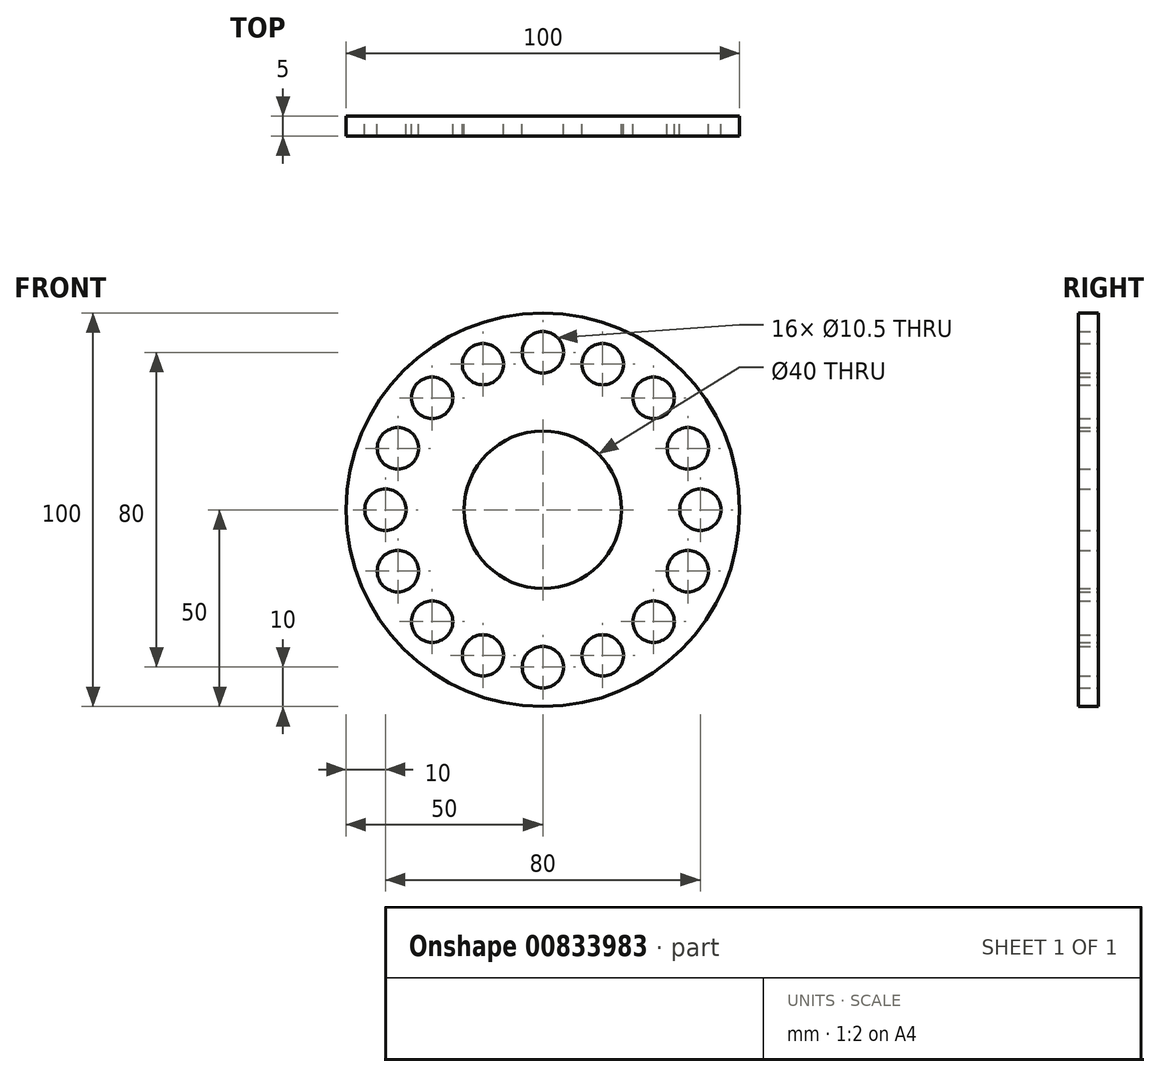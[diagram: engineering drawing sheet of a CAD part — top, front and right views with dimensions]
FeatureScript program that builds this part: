
annotation { "Feature Type Name" : "Feature", "Feature Type Description" : "" }
export const myFeature = defineFeature(function(context is Context, id is Id, definition is map)
    precondition{}
    {
        {
            var Q0;
            Q0=qCreatedBy(makeId("Front.planeOp"),FACE);
            var sketch = newSketch(context, id + "F0", { "sketchPlane" : qUnion([Q0])});
            skCircle(sketch, "E0", {"center": v(0, 0) * mm, "radius": 50 * mm});
            skCircle(sketch, "E1", {"center": v(0, 0) * mm, "radius": 20 * mm});
            skPoint(sketch, "E2", {"position": v(0, 40) * mm});
            skPoint(sketch, "E3", {"position": v(-40, 0) * mm});
            skPoint(sketch, "E4", {"position": v(0, -40) * mm});
            skPoint(sketch, "E5", {"position": v(40, 0) * mm});
            skPoint(sketch, "E6", {"position": v(15.2, 37) * mm});
            skPoint(sketch, "E7", {"position": v(28.13, 28.44) * mm});
            skPoint(sketch, "E8", {"position": v(36.83, 15.6) * mm});
            skPoint(sketch, "E9.MirrorP", {"position": v(-36.83, 15.6) * mm});
            skPoint(sketch, "E10.MirrorP", {"position": v(-15.2, 37) * mm});
            skPoint(sketch, "E11.MirrorP", {"position": v(-28.13, 28.44) * mm});
            skPoint(sketch, "E12.MirrorP", {"position": v(-28.13, -28.44) * mm});
            skPoint(sketch, "E13.MirrorP", {"position": v(-36.83, -15.6) * mm});
            skPoint(sketch, "E14.MirrorP", {"position": v(15.2, -37) * mm});
            skPoint(sketch, "E15.MirrorP", {"position": v(-15.2, -37) * mm});
            skPoint(sketch, "E16.MirrorP", {"position": v(28.13, -28.44) * mm});
            skPoint(sketch, "E17.MirrorP", {"position": v(36.83, -15.6) * mm});
            skCircle(sketch, "E18", {"center": v(-15.2, 37) * mm, "radius": 5.25 * mm});
            skCircle(sketch, "E19", {"center": v(-28.13, 28.44) * mm, "radius": 5.25 * mm});
            skCircle(sketch, "E20", {"center": v(-36.83, 15.6) * mm, "radius": 5.25 * mm});
            skCircle(sketch, "E21", {"center": v(-40, 0) * mm, "radius": 5.25 * mm});
            skCircle(sketch, "E22", {"center": v(0, 40) * mm, "radius": 5.25 * mm});
            skCircle(sketch, "E23", {"center": v(15.2, 37) * mm, "radius": 5.25 * mm});
            skCircle(sketch, "E24", {"center": v(28.13, 28.44) * mm, "radius": 5.25 * mm});
            skCircle(sketch, "E25", {"center": v(36.83, 15.6) * mm, "radius": 5.25 * mm});
            skCircle(sketch, "E26", {"center": v(40, 0) * mm, "radius": 5.25 * mm});
            skCircle(sketch, "E27.MirrorC", {"center": v(36.83, -15.6) * mm, "radius": 5.25 * mm});
            skCircle(sketch, "E28.MirrorC", {"center": v(15.2, -37) * mm, "radius": 5.25 * mm});
            skCircle(sketch, "E29.MirrorC", {"center": v(-15.2, -37) * mm, "radius": 5.25 * mm});
            skCircle(sketch, "E30.MirrorC", {"center": v(28.13, -28.44) * mm, "radius": 5.25 * mm});
            skCircle(sketch, "E31.MirrorC", {"center": v(-36.83, -15.6) * mm, "radius": 5.25 * mm});
            skCircle(sketch, "E32.MirrorC", {"center": v(0, -40) * mm, "radius": 5.25 * mm});
            skCircle(sketch, "E33.MirrorC", {"center": v(-28.13, -28.44) * mm, "radius": 5.25 * mm});
            skSolve(sketch);
        }
        {
            var Q0;
            Q0=makeQuery(id+"F0.imprint","IMPRINT",FACE,{"disambiguationData":[TD([[makeQuery(id+"F0.imprint","IMPRINT",EDGE,{"derivedFrom":sQuery(id+"F0.wireOp",EDGE,"E0")}),1.0]])]});
            var Q1;
            Q1=makeQuery(id+"F0.imprint","IMPRINT",FACE,{"disambiguationData":[TD([[makeQuery(id+"F0.imprint","IMPRINT",EDGE,{"derivedFrom":sQuery(id+"F0.wireOp",EDGE,"E1")}),-1.0]])]});
            extrude(context, id + "F1", {"entities" : qUnion([Q0, Q1]), "depth" : 5 * mm, "offsetDistance" : 25 * mm});
        }
    });
